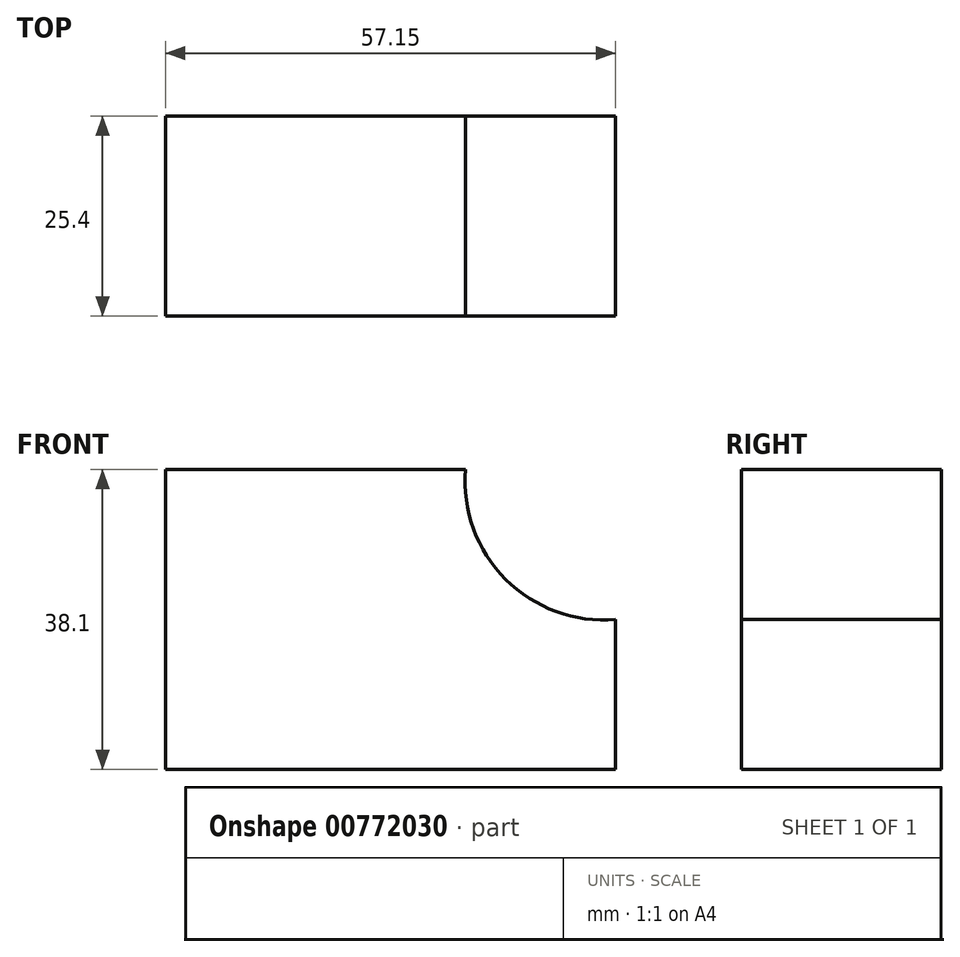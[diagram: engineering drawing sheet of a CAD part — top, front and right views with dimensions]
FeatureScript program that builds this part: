
annotation { "Feature Type Name" : "Feature", "Feature Type Description" : "" }
export const myFeature = defineFeature(function(context is Context, id is Id, definition is map)
    precondition{}
    {
        {
            var Q0;
            Q0=qCreatedBy(makeId("Front.planeOp"),FACE);
            var sketch = newSketch(context, id + "F0", { "sketchPlane" : qUnion([Q0])});
            skLineSegment(sketch, "E0.bottom", {"start": v(0, 0) * mm, "end": v(57.15, 0) * mm});
            skLineSegment(sketch, "E0.top", {"start": v(0, 38.1) * mm, "end": v(57.15, 38.1) * mm});
            skLineSegment(sketch, "E0.left", {"start": v(0, 0) * mm, "end": v(0, 38.1) * mm});
            skLineSegment(sketch, "E0.right", {"start": v(57.15, 0) * mm, "end": v(57.15, 38.1) * mm});
            skSolve(sketch);
        }
        {
            var Q0;
            Q0=makeQuery(id+"F0.imprint","IMPRINT",FACE,{"disambiguationData":[TD([[makeQuery(id+"F0.imprint","IMPRINT",EDGE,{"derivedFrom":sQuery(id+"F0.wireOp",EDGE,"E0.bottom")}),1.0]])]});
            extrude(context, id + "F1", {"entities" : qUnion([Q0]), "depth" : 25.4 * mm});
        }
        {
            var Q0;
            Q0=makeQuery(id+"F1.opExtrude","CAP_FACE",FACE,{"disambiguationData":[OSD([sQuery(id+"F0.wireOp",EDGE,"E0.bottom"),sQuery(id+"F0.wireOp",EDGE,"E0.top"),sQuery(id+"F0.wireOp",EDGE,"E0.left"),sQuery(id+"F0.wireOp",EDGE,"E0.right")])],"isStart":false});
            var sketch = newSketch(context, id + "F2", { "sketchPlane" : qUnion([Q0])});
            skArc(sketch, "E1", {"start": v(38.1, 38.1) * mm, "mid": v(43.2, 24.15) * mm, "end": v(57.15, 19.05) * mm});
            skSolve(sketch);
        }
        {
            var Q0;
            {var subQ0=sQuery(id+"F2.wireOp",EDGE,"E1");Q0=makeQuery(id+"F2.imprint","IMPRINT",FACE,{"disambiguationData":[TD([[makeQuery(id+"F2.imprint","IMPRINT",EDGE,{"derivedFrom":subQ0}),1.0]])]});}
            extrude(context, id + "F3", {"entities" : qUnion([Q0]), "operationType" : NewBodyOperationType.REMOVE, "oppositeDirection" : true, "depth" : 25.4 * mm});
        }
        {
            var Q0;
            Q0=qCreatedBy(makeId("Right.planeOp"),FACE);
            var sketch = newSketch(context, id + "F4", { "sketchPlane" : qUnion([Q0])});
            skLineSegment(sketch, "E2", {"start": v(-19.6, 38.5) * mm, "end": v(-19.6, 19.4) * mm});
            skLineSegment(sketch, "E3", {"start": v(-19.6, 19.4) * mm, "end": v(-4.52, 19.4) * mm});
            skLineSegment(sketch, "E4", {"start": v(-4.52, 19.4) * mm, "end": v(-4.52, 38.5) * mm});
            skLineSegment(sketch, "E5", {"start": v(-4.52, 38.5) * mm, "end": v(-19.6, 38.5) * mm});
            skSolve(sketch);
        }
        {
            var Q0;
            Q0 = qSketchRegion(id + "F4", true);
            extrude(context, id + "F5", {"entities" : qUnion([Q0]), "operationType" : NewBodyOperationType.REMOVE, "endBound" : BoundingType.THROUGH_ALL, "oppositeDirection" : true, "depth" : 25.4 * mm, "offsetDistance" : 25.4 * mm});
        }
        {
            var Q0;
            Q0=qCreatedBy(makeId("Right.planeOp"),FACE);
            var sketch = newSketch(context, id + "F6", { "sketchPlane" : qUnion([Q0])});
            skLineSegment(sketch, "E6", {"start": v(-18.4, 38.3) * mm, "end": v(-18.4, 24.63) * mm});
            skLineSegment(sketch, "E7", {"start": v(-18.4, 24.63) * mm, "end": v(-6.73, 24.63) * mm});
            skLineSegment(sketch, "E8", {"start": v(-6.73, 24.63) * mm, "end": v(-6.73, 37.9) * mm});
            skLineSegment(sketch, "E9", {"start": v(-6.73, 37.9) * mm, "end": v(-18.4, 38.3) * mm});
            skSolve(sketch);
        }
        {
            var Q0;
            Q0 = qSketchRegion(id + "F6", true);
            extrude(context, id + "F7", {"entities" : qUnion([Q0]), "operationType" : NewBodyOperationType.REMOVE, "endBound" : BoundingType.THROUGH_ALL, "oppositeDirection" : true, "depth" : 25.4 * mm, "offsetDistance" : 25.4 * mm});
        }
        {
            var Q0;
            Q0=qCreatedBy(makeId("Right.planeOp"),FACE);
            var sketch = newSketch(context, id + "F8", { "sketchPlane" : qUnion([Q0])});
            skLineSegment(sketch, "E10", {"start": v(-17.6, 38.3) * mm, "end": v(-17.6, 19) * mm});
            skLineSegment(sketch, "E11", {"start": v(-17.6, 19) * mm, "end": v(-4.93, 19) * mm});
            skLineSegment(sketch, "E12", {"start": v(-4.93, 19) * mm, "end": v(-4.93, 38.3) * mm});
            skLineSegment(sketch, "E13", {"start": v(-4.93, 38.3) * mm, "end": v(-17.6, 38.3) * mm});
            skSolve(sketch);
        }
        {
            var Q0;
            Q0 = qSketchRegion(id + "F8", true);
            extrude(context, id + "F9", {"entities" : qUnion([Q0]), "operationType" : NewBodyOperationType.REMOVE, "endBound" : BoundingType.THROUGH_ALL, "oppositeDirection" : true, "depth" : 25.4 * mm, "offsetDistance" : 25.4 * mm});
        }
    });
